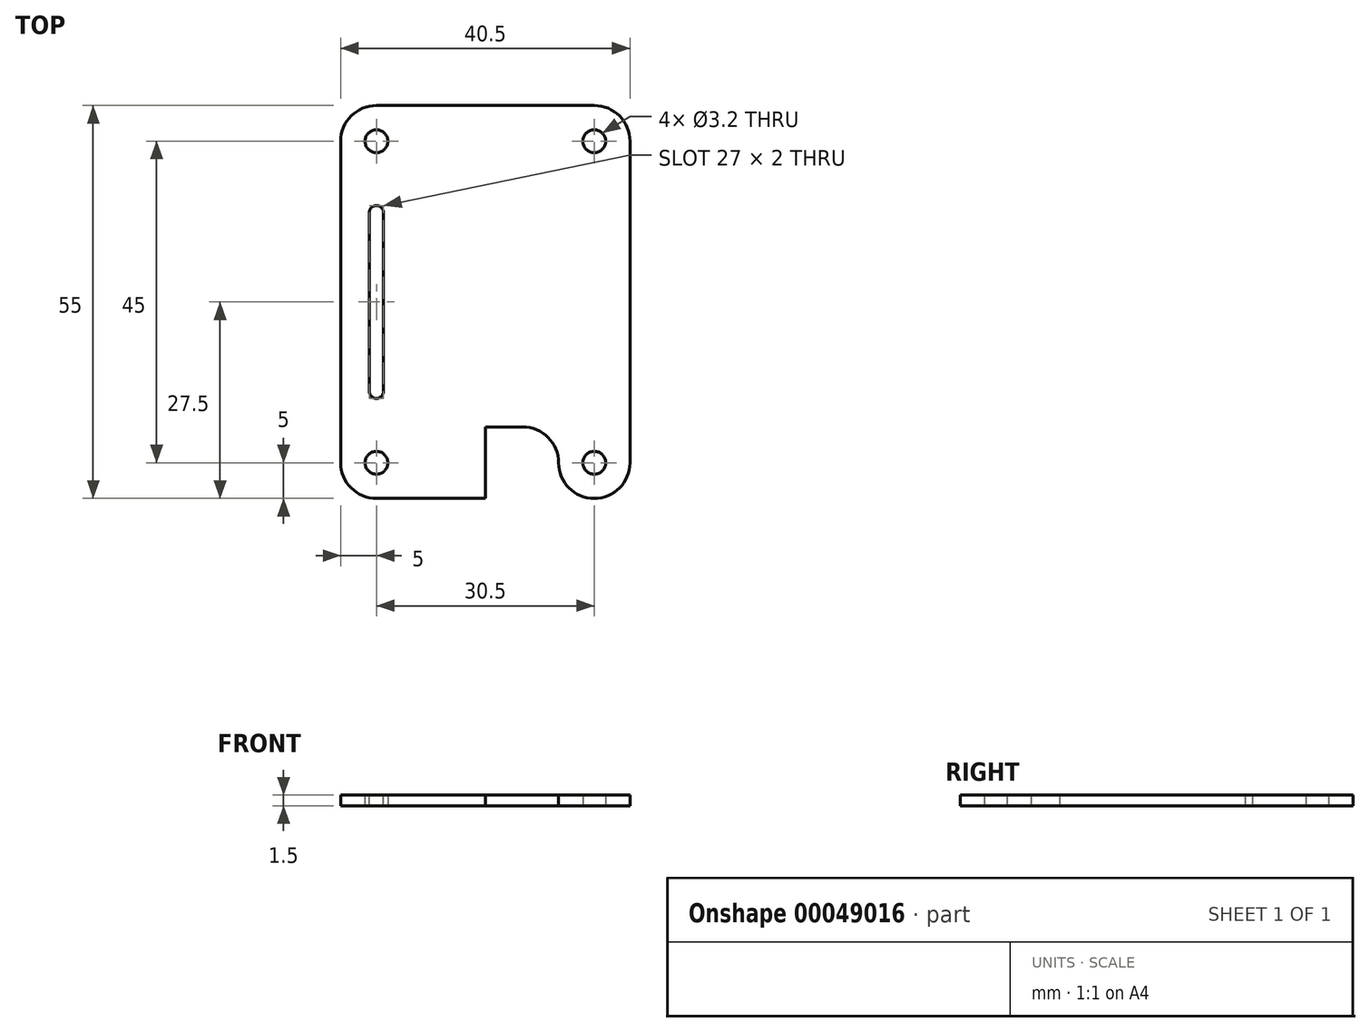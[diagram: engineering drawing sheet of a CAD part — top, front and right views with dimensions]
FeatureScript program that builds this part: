
annotation { "Feature Type Name" : "Feature", "Feature Type Description" : "" }
export const myFeature = defineFeature(function(context is Context, id is Id, definition is map)
    precondition{}
    {
        {
            var Q0;
            Q0=qCreatedBy(makeId("Top.planeOp"),FACE);
            var sketch = newSketch(context, id + "F0", { "sketchPlane" : qUnion([Q0])});
            skLineSegment(sketch, "E0.bottom", {"start": v(15.25, 27.5) * mm, "end": v(-15.25, 27.5) * mm});
            skLineSegment(sketch, "E0.top", {"start": v(15.25, -27.5) * mm, "end": v(-15.25, -27.5) * mm});
            skLineSegment(sketch, "E0.left", {"start": v(20.25, 22.5) * mm, "end": v(20.25, -22.5) * mm});
            skLineSegment(sketch, "E0.right", {"start": v(-20.25, 22.5) * mm, "end": v(-20.25, -22.5) * mm});
            skPoint(sketch, "E0.middle", {"position": v(0, 0) * mm});
            skPoint(sketch, "E1.visualSharp", {"position": v(-20.25, 27.5) * mm});
            skArc(sketch, "E1.filletArc", {"start": v(-15.25, 27.5) * mm, "mid": v(-18.79, 26.04) * mm, "end": v(-20.25, 22.5) * mm});
            skPoint(sketch, "E2.visualSharp", {"position": v(20.25, 27.5) * mm});
            skArc(sketch, "E2.filletArc", {"start": v(20.25, 22.5) * mm, "mid": v(18.79, 26.04) * mm, "end": v(15.25, 27.5) * mm});
            skPoint(sketch, "E3.visualSharp", {"position": v(20.25, -27.5) * mm});
            skArc(sketch, "E3.filletArc", {"start": v(15.25, -27.5) * mm, "mid": v(18.79, -26.04) * mm, "end": v(20.25, -22.5) * mm});
            skPoint(sketch, "E4.visualSharp", {"position": v(-20.25, -27.5) * mm});
            skArc(sketch, "E4.filletArc", {"start": v(-20.25, -22.5) * mm, "mid": v(-18.79, -26.04) * mm, "end": v(-15.25, -27.5) * mm});
            skCircle(sketch, "E5", {"center": v(-15.25, 22.5) * mm, "radius": 1.6 * mm});
            skCircle(sketch, "E6", {"center": v(15.25, 22.5) * mm, "radius": 1.6 * mm});
            skCircle(sketch, "E7", {"center": v(-15.25, -22.5) * mm, "radius": 1.6 * mm});
            skCircle(sketch, "E8", {"center": v(15.25, -22.5) * mm, "radius": 1.6 * mm});
            skSolve(sketch);
        }
        {
            var Q0;
            Q0 = qSketchRegion(id + "F0", true);
            extrude(context, id + "F1", {"entities" : qUnion([Q0]), "depth" : 1.5 * mm});
        }
        {
            var Q0;
            Q0=makeQuery(id+"F1.opExtrude","CAP_FACE",FACE,{"disambiguationData":[OSD([sQuery(id+"F0.wireOp",EDGE,"E0.bottom"),sQuery(id+"F0.wireOp",EDGE,"E0.top"),sQuery(id+"F0.wireOp",EDGE,"E0.left"),sQuery(id+"F0.wireOp",EDGE,"E0.right"),sQuery(id+"F0.wireOp",EDGE,"E1.filletArc"),sQuery(id+"F0.wireOp",EDGE,"E2.filletArc"),sQuery(id+"F0.wireOp",EDGE,"E3.filletArc"),sQuery(id+"F0.wireOp",EDGE,"E4.filletArc"),sQuery(id+"F0.wireOp",EDGE,"E5"),sQuery(id+"F0.wireOp",EDGE,"E6"),sQuery(id+"F0.wireOp",EDGE,"E7"),sQuery(id+"F0.wireOp",EDGE,"E8")])],"isStart":false});
            var sketch = newSketch(context, id + "F2", { "sketchPlane" : qUnion([Q0])});
            skLineSegment(sketch, "E9", {"start": v(-15.25, 22.5) * mm, "end": v(-15.25, 12.5) * mm, "construction": true});
            skLineSegment(sketch, "E10", {"start": v(-15.25, 12.5) * mm, "end": v(-15.25, -12.5) * mm, "construction": true});
            skLineSegment(sketch, "E11", {"start": v(-15.25, -12.5) * mm, "end": v(-15.25, -22.5) * mm, "construction": true});
            skArc(sketch, "E12", {"start": v(-14.25, 12.46) * mm, "mid": v(-15.24, 13.5) * mm, "end": v(-16.25, 12.48) * mm});
            skArc(sketch, "E13", {"start": v(-16.25, -12.5) * mm, "mid": v(-15.25, -13.5) * mm, "end": v(-14.25, -12.5) * mm});
            skLineSegment(sketch, "E14", {"start": v(-14.25, 12.54) * mm, "end": v(-14.25, -12.5) * mm});
            skLineSegment(sketch, "E15", {"start": v(-16.25, 12.52) * mm, "end": v(-16.25, -12.5) * mm});
            skSolve(sketch);
        }
        {
            var Q0;
            Q0 = qSketchRegion(id + "F2", true);
            extrude(context, id + "F3", {"entities" : qUnion([Q0]), "operationType" : NewBodyOperationType.REMOVE, "oppositeDirection" : true, "depth" : 25 * mm});
        }
        {
            var Q0;
            Q0=makeQuery(id+"F1.opExtrude","CAP_FACE",FACE,{"disambiguationData":[OSD([sQuery(id+"F0.wireOp",EDGE,"E0.bottom"),sQuery(id+"F0.wireOp",EDGE,"E0.top"),sQuery(id+"F0.wireOp",EDGE,"E0.left"),sQuery(id+"F0.wireOp",EDGE,"E0.right"),sQuery(id+"F0.wireOp",EDGE,"E1.filletArc"),sQuery(id+"F0.wireOp",EDGE,"E2.filletArc"),sQuery(id+"F0.wireOp",EDGE,"E3.filletArc"),sQuery(id+"F0.wireOp",EDGE,"E4.filletArc"),sQuery(id+"F0.wireOp",EDGE,"E5"),sQuery(id+"F0.wireOp",EDGE,"E6"),sQuery(id+"F0.wireOp",EDGE,"E7"),sQuery(id+"F0.wireOp",EDGE,"E8")])],"isStart":false});
            var sketch = newSketch(context, id + "F4", { "sketchPlane" : qUnion([Q0])});
            skLineSegment(sketch, "E16.top", {"start": v(0, -17.5) * mm, "end": v(5.25, -17.5) * mm});
            skLineSegment(sketch, "E16.right", {"start": v(10.25, -22.5) * mm, "end": v(10.25, -22.5) * mm});
            skLineSegment(sketch, "E17.top", {"start": v(0, -33.43) * mm, "end": v(15.25, -33.43) * mm});
            skLineSegment(sketch, "E17.right", {"start": v(15.25, -27.5) * mm, "end": v(15.25, -33.43) * mm});
            skLineSegment(sketch, "E18", {"start": v(15.25, -22.5) * mm, "end": v(10.25, -22.5) * mm, "construction": true});
            skPoint(sketch, "E19.visualSharp", {"position": v(-10.25, -17.5) * mm});
            skPoint(sketch, "E20.visualSharp", {"position": v(10.25, -17.5) * mm});
            skArc(sketch, "E20.filletArc", {"start": v(10.25, -22.5) * mm, "mid": v(8.79, -18.96) * mm, "end": v(5.25, -17.5) * mm});
            skLineSegment(sketch, "E21.trimOffspring", {"start": v(15.25, -27.5) * mm, "end": v(15.25, -27.5) * mm});
            skPoint(sketch, "E22.visualSharp", {"position": v(10.25, -27.5) * mm});
            skArc(sketch, "E22.filletArc", {"start": v(10.25, -22.5) * mm, "mid": v(11.71, -26.04) * mm, "end": v(15.25, -27.5) * mm});
            skLineSegment(sketch, "E23", {"start": v(0, -17.5) * mm, "end": v(0, -27.5) * mm});
            skPoint(sketch, "E19.filletArc.start.orphan", {"position": v(-5.25, -17.5) * mm});
            skPoint(sketch, "E24.start.orphan", {"position": v(-15.25, -22.5) * mm});
            skLineSegment(sketch, "E25", {"start": v(0, -27.5) * mm, "end": v(0, -33.43) * mm});
            skPoint(sketch, "E26.orphan", {"position": v(-15.25, -33.43) * mm});
            skSolve(sketch);
        }
        {
            var Q0;
            Q0 = qSketchRegion(id + "F4", true);
            extrude(context, id + "F5", {"entities" : qUnion([Q0]), "operationType" : NewBodyOperationType.REMOVE, "oppositeDirection" : true, "depth" : 25 * mm});
        }
    });
